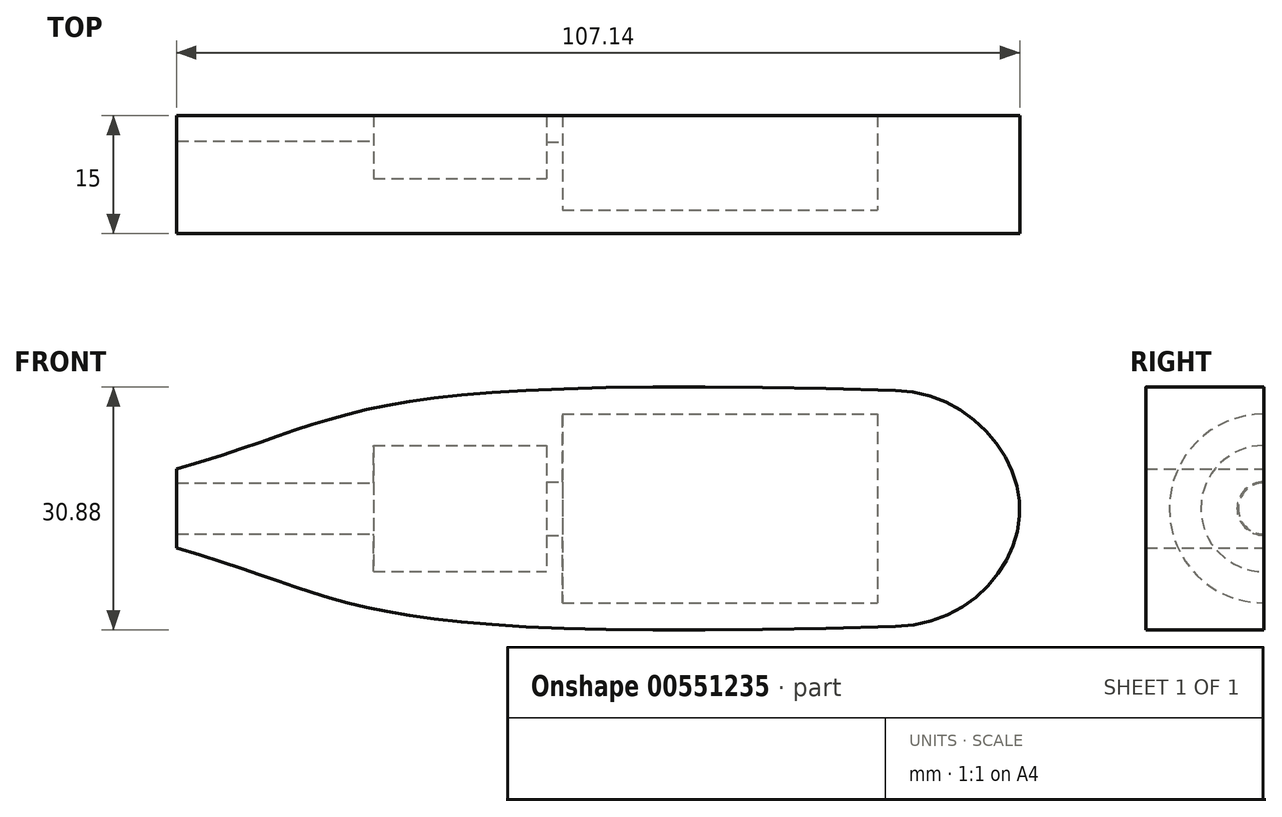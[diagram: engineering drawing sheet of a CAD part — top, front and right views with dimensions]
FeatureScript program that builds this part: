
annotation { "Feature Type Name" : "Feature", "Feature Type Description" : "" }
export const myFeature = defineFeature(function(context is Context, id is Id, definition is map)
    precondition{}
    {
        {
            var Q0;
            Q0=qCreatedBy(makeId("Front.planeOp"),FACE);
            var sketch = newSketch(context, id + "F0", { "sketchPlane" : qUnion([Q0])});
            skLineSegment(sketch, "E0", {"start": v(-49, 3.25) * mm, "end": v(-24, 3.25) * mm});
            skLineSegment(sketch, "E1", {"start": v(-24, 3.25) * mm, "end": v(-24, 8) * mm});
            skLineSegment(sketch, "E2", {"start": v(-24, 8) * mm, "end": v(-2, 8) * mm});
            skLineSegment(sketch, "E3", {"start": v(-2, 8) * mm, "end": v(-2, 3.4) * mm});
            skLineSegment(sketch, "E4", {"start": v(-2, 3.4) * mm, "end": v(0, 3.4) * mm});
            skLineSegment(sketch, "E5", {"start": v(0, 3.4) * mm, "end": v(0, 12) * mm});
            skLineSegment(sketch, "E6", {"start": v(0, 12) * mm, "end": v(40, 12) * mm});
            skLineSegment(sketch, "E7", {"start": v(40, 12) * mm, "end": v(40, 0) * mm});
            skLineSegment(sketch, "E8", {"start": v(40, 0) * mm, "end": v(-49, 0) * mm});
            skLineSegment(sketch, "E9", {"start": v(-49, 0) * mm, "end": v(-49, 3.25) * mm});
            skSolve(sketch);
        }
        {
            var Q0;
            Q0=makeQuery(id+"F0.imprint","IMPRINT",FACE,{"disambiguationData":[TD([[makeQuery(id+"F0.imprint","IMPRINT",EDGE,{"derivedFrom":sQuery(id+"F0.wireOp",EDGE,"E0")}),-1.0]])]});
            var Q1;
            Q1=sQuery(id+"F0.wireOp",EDGE,"E8");
            revolve(context, id + "F1", {"entities" : qUnion([Q0]), "axis" : qUnion([Q1]), "revolveType" : RevolveType.FULL});
        }
        {
            var Q0;
            Q0=qCreatedBy(makeId("Front.planeOp"),FACE);
            var sketch = newSketch(context, id + "F2", { "sketchPlane" : qUnion([Q0])});
            skLineSegment(sketch, "E10", {"start": v(-49.04, 5) * mm, "end": v(-49.04, -5) * mm});
            skFitSpline(sketch, "E11", {"points": [v(-49.04, 5) * mm, v(42.3, 15) * mm], "startDerivative": vector(73.02, 20.8) * mm, "endDerivative": vector(213.22, -6) * mm});
            skFitSpline(sketch, "E12.MirrorCS", {"points": [v(-49.04, -5) * mm, v(42.3, -15) * mm], "startDerivative": vector(73.02, -20.8) * mm, "endDerivative": vector(213.22, 6) * mm});
            skFitSpline(sketch, "E13", {"points": [v(42.3, 15) * mm, v(58.1, 0) * mm, v(42.3, -15) * mm], "startDerivative": vector(52.49, -0.98) * mm, "endDerivative": vector(-54.88, -1.03) * mm});
            skSolve(sketch);
        }
        {
            var Q0;
            Q0=makeQuery(id+"F2.imprint","IMPRINT",FACE,{"disambiguationData":[TD([[makeQuery(id+"F2.imprint","IMPRINT",EDGE,{"derivedFrom":sQuery(id+"F2.wireOp",EDGE,"E10")}),1.0]])]});
            extrude(context, id + "F3", {"entities" : qUnion([Q0]), "depth" : 15 * mm, "offsetDistance" : 25 * mm});
        }
        {
            var Q0;
            Q0=makeQuery(id+"F1.opRevolve","SWEPT_BODY",BODY,{"disambiguationData":[OSD([sQuery(id+"F0.wireOp",EDGE,"E0"),sQuery(id+"F0.wireOp",EDGE,"E1"),sQuery(id+"F0.wireOp",EDGE,"E2"),sQuery(id+"F0.wireOp",EDGE,"E3"),sQuery(id+"F0.wireOp",EDGE,"E4"),sQuery(id+"F0.wireOp",EDGE,"E5"),sQuery(id+"F0.wireOp",EDGE,"E6"),sQuery(id+"F0.wireOp",EDGE,"E7"),sQuery(id+"F0.wireOp",EDGE,"E8"),sQuery(id+"F0.wireOp",EDGE,"E9")])]});
            var Q1;
            Q1=makeQuery(id+"F3.opExtrude","SWEPT_BODY",BODY,{"disambiguationData":[OSD([sQuery(id+"F2.wireOp",EDGE,"E10"),sQuery(id+"F2.wireOp",EDGE,"E11"),sQuery(id+"F2.wireOp",EDGE,"E12.MirrorCS"),sQuery(id+"F2.wireOp",EDGE,"E13")])]});
            booleanBodies(context, id + "F4", {"operationType" : BooleanOperationType.SUBTRACTION, "tools" : qUnion([Q0]), "targets" : qUnion([Q1])});
        }
    });
